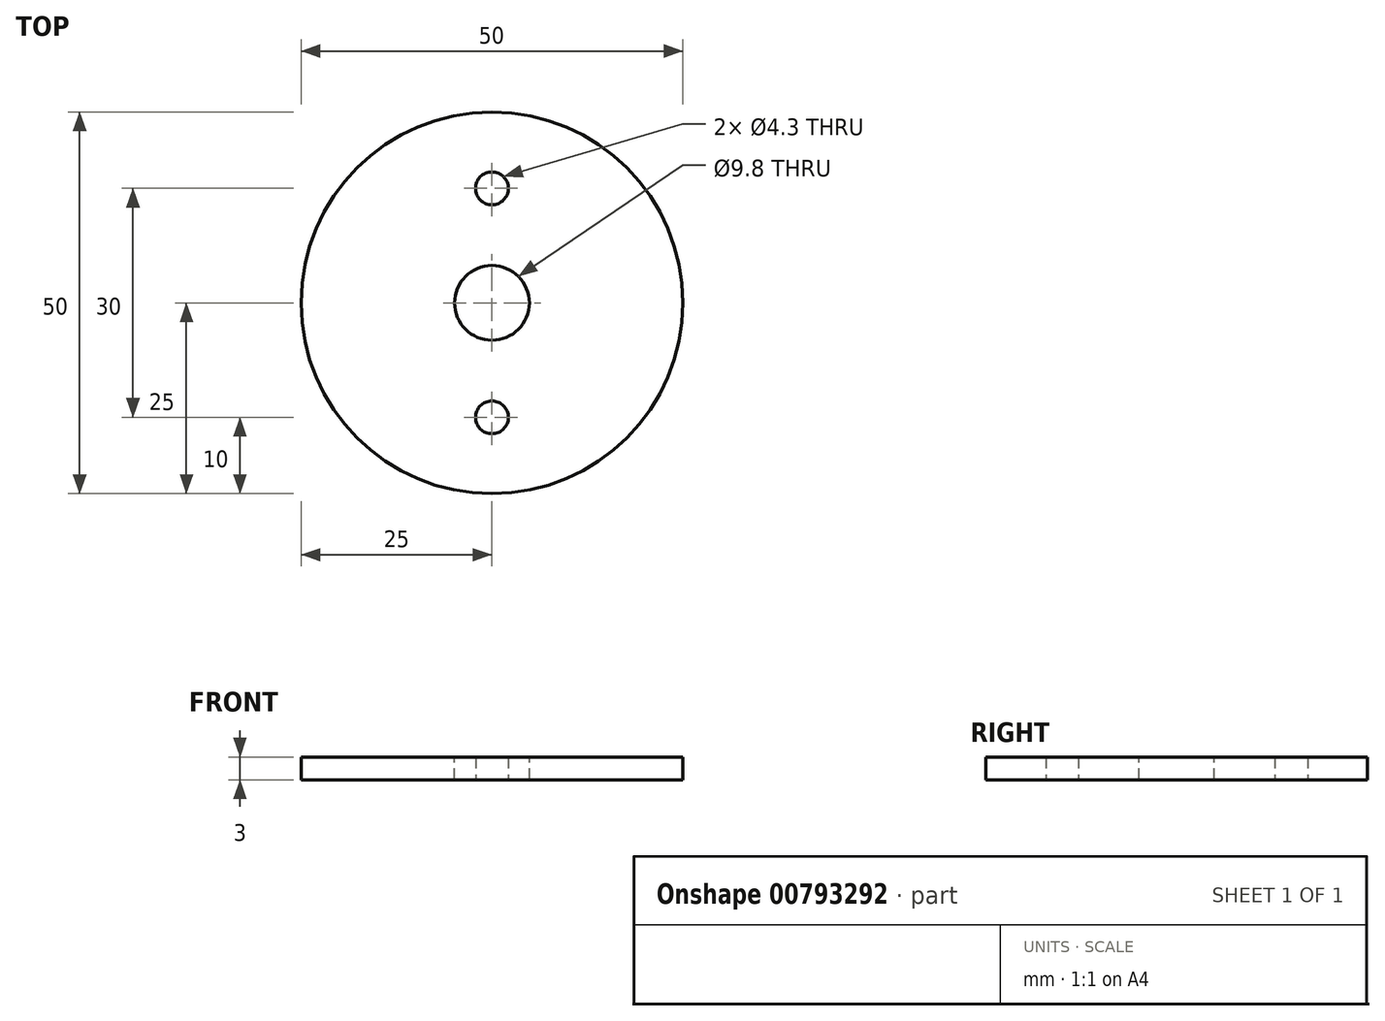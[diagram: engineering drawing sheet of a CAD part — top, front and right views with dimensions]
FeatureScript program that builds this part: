
annotation { "Feature Type Name" : "Feature", "Feature Type Description" : "" }
export const myFeature = defineFeature(function(context is Context, id is Id, definition is map)
    precondition{}
    {
        {
            var Q0;
            Q0=qCreatedBy(makeId("Top.planeOp"),FACE);
            var sketch = newSketch(context, id + "F0", { "sketchPlane" : qUnion([Q0])});
            skCircle(sketch, "E0", {"center": v(0, 0) * mm, "radius": 25 * mm});
            skCircle(sketch, "E1", {"center": v(0, 15) * mm, "radius": 2.15 * mm});
            skCircle(sketch, "E2", {"center": v(0, -15) * mm, "radius": 2.15 * mm});
            skSolve(sketch);
        }
        {
            var Q0;
            Q0=qSketchRegion(id+"F0",true);
            extrude(context, id + "F1", {"entities" : qUnion([Q0]), "depth" : 3 * mm, "offsetDistance" : 25 * mm});
        }
        {
            var Q0;
            Q0=makeQuery(id+"F1.opExtrude","CAP_FACE",FACE,{"disambiguationData":[OSD([sQuery(id+"F0.wireOp",EDGE,"E0"),sQuery(id+"F0.wireOp",EDGE,"E1"),sQuery(id+"F0.wireOp",EDGE,"E2")])],"isStart":false});
            var sketch = newSketch(context, id + "F2", { "sketchPlane" : qUnion([Q0])});
            skCircle(sketch, "E3", {"center": v(0, 0) * mm, "radius": 4.9 * mm});
            skSolve(sketch);
        }
        {
            var Q0;
            Q0=qSketchRegion(id+"F2",true);
            extrude(context, id + "F3", {"entities" : qUnion([Q0]), "operationType" : NewBodyOperationType.REMOVE, "endBound" : BoundingType.THROUGH_ALL, "oppositeDirection" : true, "depth" : 25 * mm, "offsetDistance" : 25 * mm});
        }
    });
